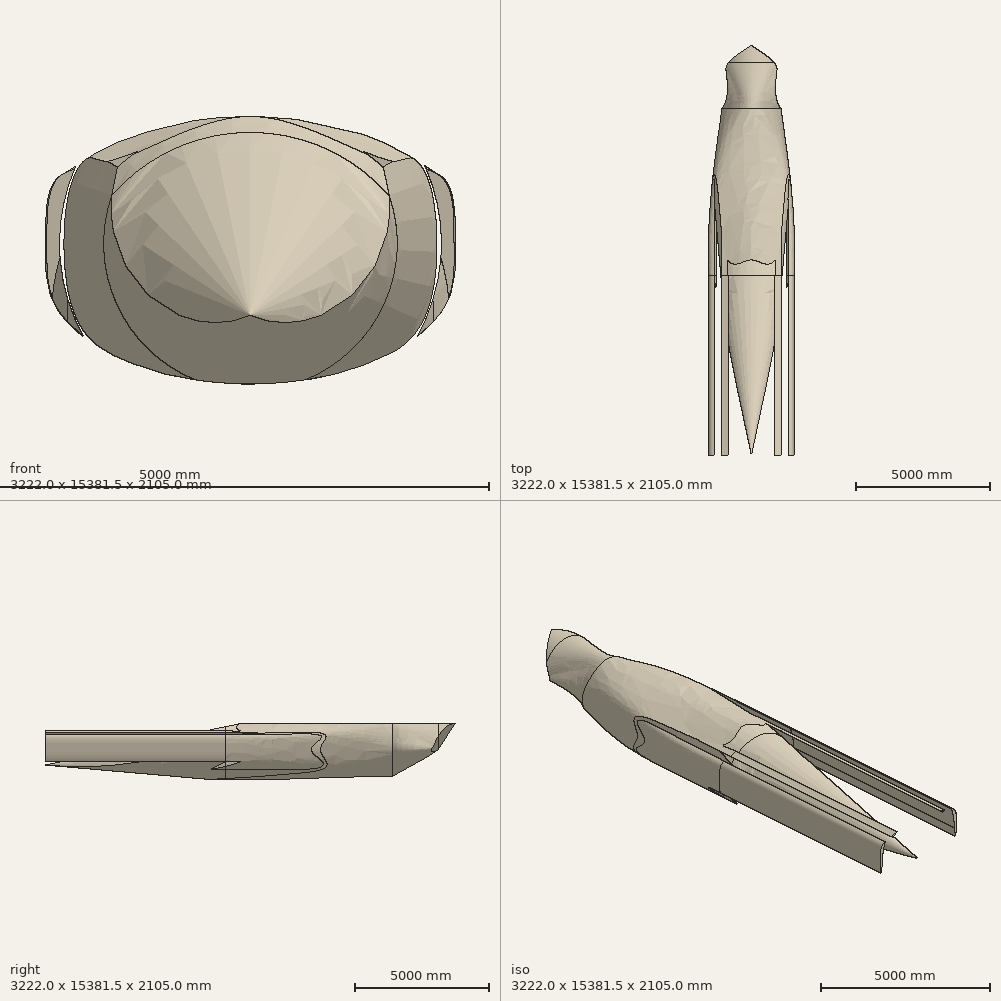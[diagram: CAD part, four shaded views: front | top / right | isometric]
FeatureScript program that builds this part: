
annotation { "Feature Type Name" : "Feature", "Feature Type Description" : "" }
export const myFeature = defineFeature(function(context is Context, id is Id, definition is map)
    precondition{}
    {
        {
            var Q0;
            Q0=qCreatedBy(makeId("Front.planeOp"),FACE);
            cPlane(context, id + "F0", {"entities" : qUnion([Q0]), "cplaneType" : CPlaneType.OFFSET, "offset" : 1750 * mm, "width" : 152.4 * mm, "height" : 152.4 * mm});
        }
        {
            var Q0;
            Q0=qCreatedBy(id+"F0.planeOp",FACE);
            var sketch = newSketch(context, id + "F1", { "sketchPlane" : qUnion([Q0])});
            skPoint(sketch, "E0.middle", {"position": v(0, 0) * mm});
            skFitSpline(sketch, "E1", {"points": [v(0, 1000) * mm, v(1060, 662.5) * mm, v(1517.6, 506.84) * mm, v(1600, 0) * mm, v(1517.6, -506.84) * mm, v(750, -1000) * mm, v(-750, -1000) * mm, v(-1517.6, -506.84) * mm, v(-1600, 0) * mm, v(-1517.6, 506.84) * mm, v(-1060, 662.5) * mm, v(0, 1000) * mm]});
            skSolve(sketch);
        }
        {
            var Q0;
            Q0=qCreatedBy(makeId("Front.planeOp"),FACE);
            var sketch = newSketch(context, id + "F2", { "sketchPlane" : qUnion([Q0])});
            skPoint(sketch, "E2.middle", {"position": v(0, 0) * mm});
            skFitSpline(sketch, "E3", {"points": [v(0, 1000) * mm, v(1060, 662.5) * mm, v(1517.6, 506.84) * mm, v(1600, 0) * mm, v(1517.6, -506.84) * mm, v(750, -1000) * mm, v(-750, -1000) * mm, v(-1517.6, -506.84) * mm, v(-1600, 0) * mm, v(-1517.6, 506.84) * mm, v(-1060, 662.5) * mm, v(0, 1000) * mm]});
            skSolve(sketch);
        }
        {
            var Q0;
            Q0=qCreatedBy(makeId("Front.planeOp"),FACE);
            cPlane(context, id + "F3", {"entities" : qUnion([Q0]), "cplaneType" : CPlaneType.OFFSET, "offset" : 3500 * mm, "oppositeDirection" : true, "width" : 150 * mm, "height" : 150 * mm});
        }
        {
            var Q0;
            Q0=qCreatedBy(id+"F3.planeOp",FACE);
            var sketch = newSketch(context, id + "F4", { "sketchPlane" : qUnion([Q0])});
            skPoint(sketch, "E4.middle", {"position": v(0, 0) * mm});
            skFitSpline(sketch, "E5", {"points": [v(0, 1000) * mm, v(1060, 662.5) * mm, v(1250, 0) * mm, v(1060, -662.5) * mm, v(0, -1000) * mm, v(-1060, -662.5) * mm, v(-1250, 0) * mm, v(-1060, 662.5) * mm, v(0, 1000) * mm]});
            skSolve(sketch);
        }
        {
            var Q0;
            Q0=qCreatedBy(makeId("Front.planeOp"),FACE);
            cPlane(context, id + "F5", {"entities" : qUnion([Q0]), "cplaneType" : CPlaneType.OFFSET, "offset" : 4500 * mm, "oppositeDirection" : true, "width" : 150 * mm, "height" : 150 * mm});
        }
        {
            var Q0;
            Q0=qCreatedBy(id+"F5.planeOp",FACE);
            var sketch = newSketch(context, id + "F6", { "sketchPlane" : qUnion([Q0])});
            skPoint(sketch, "E6.middle", {"position": v(0, 0) * mm});
            skFitSpline(sketch, "E7", {"points": [v(0, 1000) * mm, v(848, 530) * mm, v(1108.5, 0) * mm, v(848, -530) * mm, v(0, -1000) * mm, v(-848, -530) * mm, v(-1108.5, 0) * mm, v(-848, 530) * mm, v(0, 1000) * mm]});
            skSolve(sketch);
        }
        {
            var Q0;
            Q0=qCreatedBy(makeId("Front.planeOp"),FACE);
            cPlane(context, id + "F7", {"entities" : qUnion([Q0]), "cplaneType" : CPlaneType.OFFSET, "offset" : 6232.05 * mm, "oppositeDirection" : true, "width" : 150 * mm, "height" : 150 * mm});
        }
        {
            var Q0;
            Q0=qCreatedBy(id+"F7.planeOp",FACE);
            var sketch = newSketch(context, id + "F8", { "sketchPlane" : qUnion([Q0])});
            skArc(sketch, "E8", {"start": v(998.61, 52.63) * mm, "mid": v(0, 1000) * mm, "end": v(-998.61, 52.63) * mm});
            skLineSegment(sketch, "E9", {"start": v(0, 0) * mm, "end": v(-948.68, 0) * mm});
            skLineSegment(sketch, "E10", {"start": v(0, 0) * mm, "end": v(948.68, 0) * mm});
            skPoint(sketch, "E11.visualSharp", {"position": v(-1000, 0) * mm});
            skArc(sketch, "E11.filletArc", {"start": v(-998.61, 52.63) * mm, "mid": v(-984.96, 15.59) * mm, "end": v(-948.68, 0) * mm});
            skPoint(sketch, "E12.visualSharp", {"position": v(1000, 0) * mm});
            skArc(sketch, "E12.filletArc", {"start": v(948.68, 0) * mm, "mid": v(984.96, 15.59) * mm, "end": v(998.61, 52.63) * mm});
            skSolve(sketch);
        }
        {
            var Q0;
            Q0=sQuery(id+"F8.wireOp",EDGE,"E9");
            var Q1;
            Q1=sQuery(id+"F6.wireOp",VERTEX,"E7.6.internal");
            cPlane(context, id + "F9", {"entities" : qUnion([Q0, Q1]), "cplaneType" : CPlaneType.LINE_ANGLE, "offset" : 25 * mm, "angle" : 0 * degree, "width" : 150 * mm, "height" : 150 * mm});
        }
        {
            var Q0;
            Q0=qCreatedBy(id+"F9.planeOp",FACE);
            var sketch = newSketch(context, id + "F10", { "sketchPlane" : qUnion([Q0])});
            skFitSpline(sketch, "E13", {"points": [v(-1108.5, 4500) * mm, v(-948.68, 6232.05) * mm], "startDerivative": vector(1200, 1755) * mm, "endDerivative": vector(158.07, 1422.55) * mm});
            skFitSpline(sketch, "E14", {"points": [v(1108.5, 4500) * mm, v(948.68, 6232.05) * mm], "startDerivative": vector(-1200, 1755) * mm, "endDerivative": vector(-158.07, 1422.55) * mm});
            skSolve(sketch);
        }
        {
            var Q0;
            Q0=makeQuery(id+"F1.imprint","IMPRINT",FACE,{"disambiguationData":[TD([[makeQuery(id+"F1.imprint","IMPRINT",EDGE,{"derivedFrom":sQuery(id+"F1.wireOp",EDGE,"E1")}),-1.0]])]});
            var Q1;
            Q1=makeQuery(id+"F2.imprint","IMPRINT",FACE,{"disambiguationData":[TD([[makeQuery(id+"F2.imprint","IMPRINT",EDGE,{"derivedFrom":sQuery(id+"F2.wireOp",EDGE,"E3")}),-1.0]])]});
            var Q2;
            Q2=makeQuery(id+"F4.imprint","IMPRINT",FACE,{"disambiguationData":[TD([[makeQuery(id+"F4.imprint","IMPRINT",EDGE,{"derivedFrom":sQuery(id+"F4.wireOp",EDGE,"E5")}),-1.0]])]});
            var Q3;
            Q3=makeQuery(id+"F6.imprint","IMPRINT",FACE,{"disambiguationData":[TD([[makeQuery(id+"F6.imprint","IMPRINT",EDGE,{"derivedFrom":sQuery(id+"F6.wireOp",EDGE,"E7")}),-1.0]])]});
            loft(context, id + "F11", {"sheetProfilesArray" : [{ "sheetProfileEntities" : qUnion([Q0]) }, { "sheetProfileEntities" : qUnion([Q1]) }, { "sheetProfileEntities" : qUnion([Q2]) }, { "sheetProfileEntities" : qUnion([Q3]) }]});
        }
        {
            var Q1;
            Q1=makeQuery(id+"F6.imprint","IMPRINT",FACE,{"disambiguationData":[TD([[makeQuery(id+"F6.imprint","IMPRINT",EDGE,{"derivedFrom":sQuery(id+"F6.wireOp",EDGE,"E7")}),-1.0]])]});
            var Q2;
            Q2=makeQuery(id+"F8.imprint","IMPRINT",FACE,{"disambiguationData":[TD([[makeQuery(id+"F8.imprint","IMPRINT",EDGE,{"derivedFrom":sQuery(id+"F8.wireOp",EDGE,"E8")}),1.0]])]});
            var Q3;
            Q3=sQuery(id+"F10.wireOp",EDGE,"E13");
            var Q4;
            Q4=sQuery(id+"F10.wireOp",EDGE,"E14");
            loft(context, id + "F12", {"operationType" : NewBodyOperationType.ADD, "addGuides" : true, "sheetProfilesArray" : [{ "sheetProfileEntities" : qUnion([Q1]) }, { "sheetProfileEntities" : qUnion([Q2]) }], "guidesArray" : [{ "guideEntities" : qUnion([Q3]), "guideDerivativeType" : LoftGuideDerivativeType.DEFAULT, "guideDerivativeMagnitude" : 1 }, { "guideEntities" : qUnion([Q4]), "guideDerivativeType" : LoftGuideDerivativeType.DEFAULT, "guideDerivativeMagnitude" : 1 }]});
        }
        {
            var Q0;
            Q0=makeQuery(id+"F11.opLoft","CAP_FACE",FACE,{"disambiguationData":[OSD([makeQuery(id+"F1.imprint","IMPRINT",FACE,{"disambiguationData":[TD([[makeQuery(id+"F1.imprint","IMPRINT",EDGE,{"derivedFrom":sQuery(id+"F1.wireOp",EDGE,"E1")}),-1.0]])]})])],"isStart":true});
            extrude(context, id + "F13", {"entities" : qUnion([Q0]), "depth" : 6750 * mm});
        }
        {
            var Q0;
            Q0=qCreatedBy(makeId("Right.planeOp"),FACE);
            var sketch = newSketch(context, id + "F14", { "sketchPlane" : qUnion([Q0])});
            skLineSegment(sketch, "E15", {"start": v(0, 0) * mm, "end": v(-3500, 0) * mm});
            skLineSegment(sketch, "E16", {"start": v(-3500, 0) * mm, "end": v(-3500, -1000) * mm});
            skLineSegment(sketch, "E17", {"start": v(-3500, -1000) * mm, "end": v(-8500, -1000) * mm});
            skLineSegment(sketch, "E18", {"start": v(-8500, -1000) * mm, "end": v(-8500, -562.56) * mm});
            skLineSegment(sketch, "E19", {"start": v(-1164.58, 0) * mm, "end": v(-1164.58, 1000) * mm});
            skLineSegment(sketch, "E20", {"start": v(-1164.58, 1000) * mm, "end": v(-8500, -562.56) * mm});
            skLineSegment(sketch, "E21", {"start": v(-8500, -562.56) * mm, "end": v(-3500, -1000) * mm});
            skLineSegment(sketch, "E22", {"start": v(-3500, 1000) * mm, "end": v(4500, 1000) * mm});
            skLineSegment(sketch, "E23", {"start": v(-3500, 1000) * mm, "end": v(-8500, 1000) * mm});
            skLineSegment(sketch, "E24", {"start": v(-8500, -1000) * mm, "end": v(-8500, -1500) * mm});
            skLineSegment(sketch, "E25", {"start": v(-3500, -1000) * mm, "end": v(2215.03, -1500) * mm});
            skLineSegment(sketch, "E26", {"start": v(2215.03, -1500) * mm, "end": v(-8500, -1500) * mm});
            skLineSegment(sketch, "E27", {"start": v(-8500, -562.56) * mm, "end": v(-3500, -562.56) * mm});
            skPoint(sketch, "E27.endSnap0", {"position": v(-3500, -500) * mm});
            skLineSegment(sketch, "E28", {"start": v(-8500, 1000) * mm, "end": v(-8500, -562.56) * mm});
            skSolve(sketch);
        }
        {
            var Q0;
            {var subQ0=sQuery(id+"F14.wireOp",EDGE,"E20");Q0=makeQuery(id+"F14.imprint","IMPRINT",FACE,{"disambiguationData":[TD([[makeQuery(id+"F14.imprint","IMPRINT",EDGE,{"derivedFrom":subQ0}),-1.0]])]});}
            var Q1;
            Q1=sQuery(id+"F14.wireOp",EDGE,"E27");
            revolve(context, id + "F15", {"operationType" : NewBodyOperationType.REMOVE, "entities" : qUnion([Q0]), "axis" : qUnion([Q1]), "revolveType" : RevolveType.SYMMETRIC, "oppositeDirection" : true, "angle" : 250 * degree});
        }
        {
            var Q0;
            Q0=makeQuery(id+"F14.imprint","IMPRINT",FACE,{"disambiguationData":[TD([[makeQuery(id+"F14.imprint","IMPRINT",EDGE,{"derivedFrom":sQuery(id+"F14.wireOp",EDGE,"E17")}),-1.0]])]});
            var Q1;
            Q1=makeQuery(id+"F14.imprint","IMPRINT",FACE,{"disambiguationData":[TD([[makeQuery(id+"F14.imprint","IMPRINT",EDGE,{"derivedFrom":sQuery(id+"F14.wireOp",EDGE,"E17")}),1.0]])]});
            var Q2;
            Q2=sQuery(id+"F14.wireOp",EDGE,"E15");
            revolve(context, id + "F16", {"operationType" : NewBodyOperationType.REMOVE, "entities" : qUnion([Q0, Q1]), "axis" : qUnion([Q2]), "revolveType" : RevolveType.SYMMETRIC, "oppositeDirection" : true, "angle" : 240 * degree});
        }
        {
            var Q0;
            Q0=makeQuery(id+"F12.opLoft","CAP_FACE",FACE,{"disambiguationData":[OSD([makeQuery(id+"F8.imprint","IMPRINT",FACE,{"disambiguationData":[TD([[makeQuery(id+"F8.imprint","IMPRINT",EDGE,{"derivedFrom":sQuery(id+"F8.wireOp",EDGE,"E8")}),1.0]])]})])],"isStart":true});
            extrude(context, id + "F17", {"entities" : qUnion([Q0]), "operationType" : NewBodyOperationType.ADD, "depth" : 649.4 * mm});
        }
        {
            var Q0;
            Q0=qCreatedBy(makeId("Right.planeOp"),FACE);
            var sketch = newSketch(context, id + "F18", { "sketchPlane" : qUnion([Q0])});
            skLineSegment(sketch, "E29", {"start": v(0, 0) * mm, "end": v(4500, 0) * mm});
            skLineSegment(sketch, "E30", {"start": v(4500, 0) * mm, "end": v(6232.05, 0) * mm});
            skLineSegment(sketch, "E31", {"start": v(4500, 0) * mm, "end": v(4500, 1000) * mm});
            skLineSegment(sketch, "E32", {"start": v(4500, 1000) * mm, "end": v(6881.46, 1000) * mm});
            skLineSegment(sketch, "E33", {"start": v(6881.46, 1000) * mm, "end": v(6881.46, -1000) * mm});
            skLineSegment(sketch, "E34", {"start": v(6881.46, 1000) * mm, "end": v(6232.05, 0) * mm});
            skLineSegment(sketch, "E35", {"start": v(6232.05, 0) * mm, "end": v(5582.64, -1000) * mm});
            skLineSegment(sketch, "E36", {"start": v(5582.64, -1000) * mm, "end": v(6881.46, -1000) * mm});
            skSolve(sketch);
        }
        {
            var Q0;
            Q0=makeQuery(id+"F18.imprint","IMPRINT",FACE,{"disambiguationData":[TD([[makeQuery(id+"F18.imprint","IMPRINT",EDGE,{"derivedFrom":sQuery(id+"F18.wireOp",EDGE,"E33")}),-1.0]])]});
            var Q1;
            Q1=sQuery(id+"F18.wireOp",EDGE,"E32");
            revolve(context, id + "F19", {"operationType" : NewBodyOperationType.REMOVE, "entities" : qUnion([Q0]), "axis" : qUnion([Q1]), "revolveType" : RevolveType.SYMMETRIC, "oppositeDirection" : true, "angle" : 182 * degree});
        }
    });
